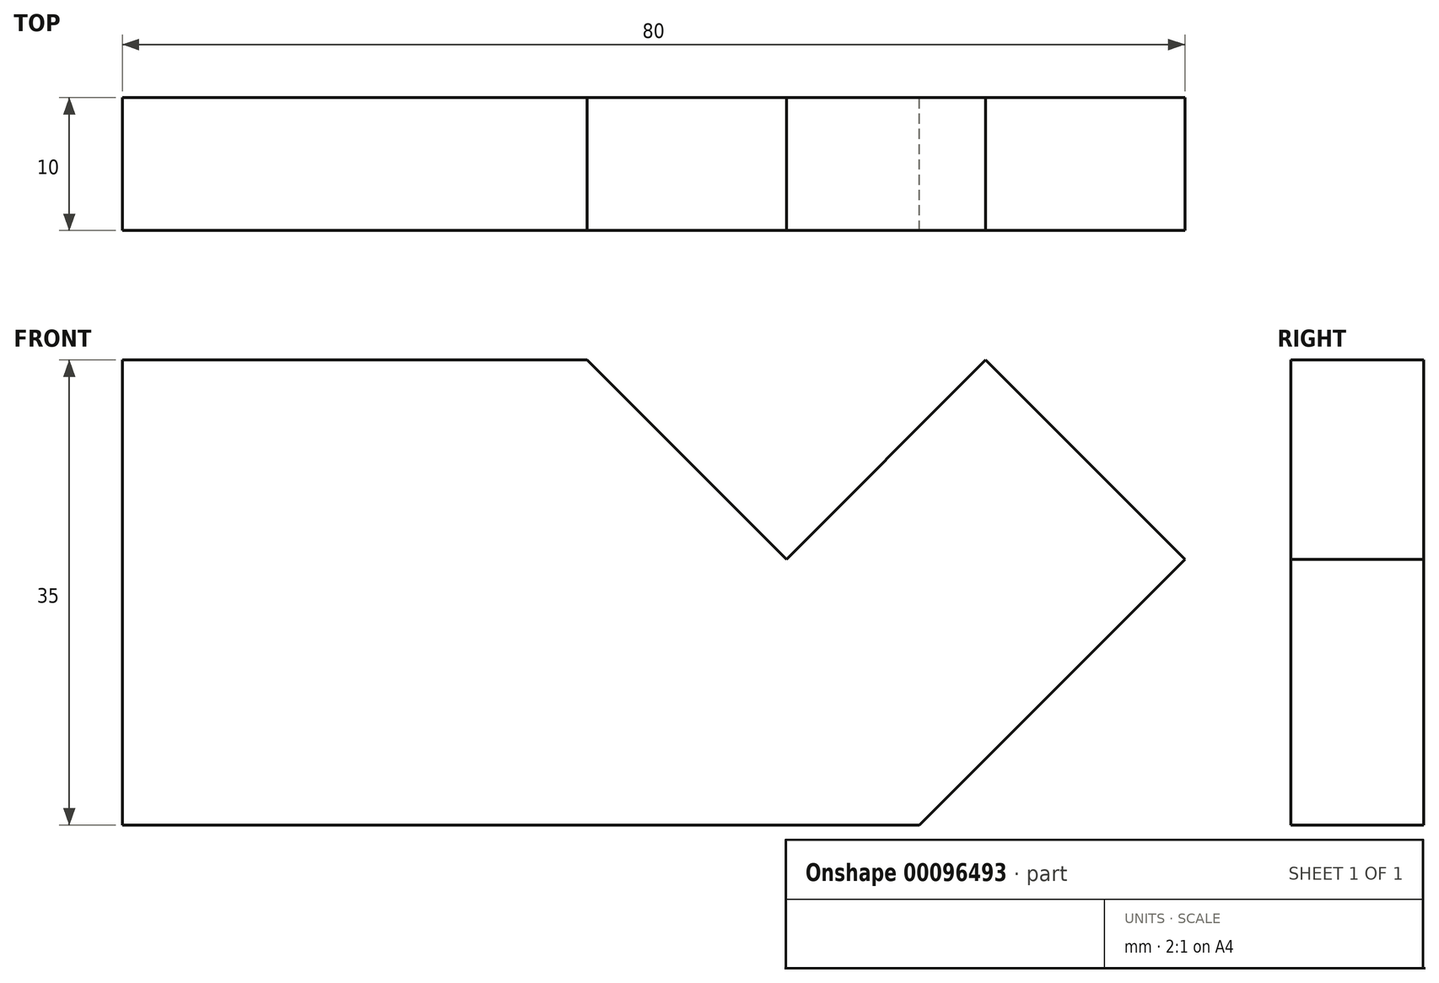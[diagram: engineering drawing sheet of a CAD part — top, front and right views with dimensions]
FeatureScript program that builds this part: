
annotation { "Feature Type Name" : "Feature", "Feature Type Description" : "" }
export const myFeature = defineFeature(function(context is Context, id is Id, definition is map)
    precondition{}
    {
        {
            var Q0;
            Q0=qCreatedBy(makeId("Front.planeOp"),FACE);
            var sketch = newSketch(context, id + "F0", { "sketchPlane" : qUnion([Q0])});
            skLineSegment(sketch, "E0", {"start": v(0, 0) * mm, "end": v(0, 35) * mm});
            skLineSegment(sketch, "E1", {"start": v(0, 35) * mm, "end": v(35, 35) * mm});
            skLineSegment(sketch, "E2", {"start": v(35, 35) * mm, "end": v(50, 20) * mm});
            skLineSegment(sketch, "E3", {"start": v(60, 0) * mm, "end": v(0, 0) * mm});
            skLineSegment(sketch, "E4", {"start": v(50, 20) * mm, "end": v(65, 35) * mm});
            skLineSegment(sketch, "E5", {"start": v(65, 35) * mm, "end": v(80, 20) * mm});
            skLineSegment(sketch, "E6", {"start": v(80, 20) * mm, "end": v(60, 0) * mm});
            skSolve(sketch);
        }
        {
            var Q0;
            Q0=makeQuery(id+"F0.imprint","IMPRINT",FACE,{"disambiguationData":[TD([[makeQuery(id+"F0.imprint","IMPRINT",EDGE,{"derivedFrom":sQuery(id+"F0.wireOp",EDGE,"E0")}),-1.0]])]});
            extrude(context, id + "F1", {"entities" : qUnion([Q0]), "depth" : 10 * mm});
        }
    });
